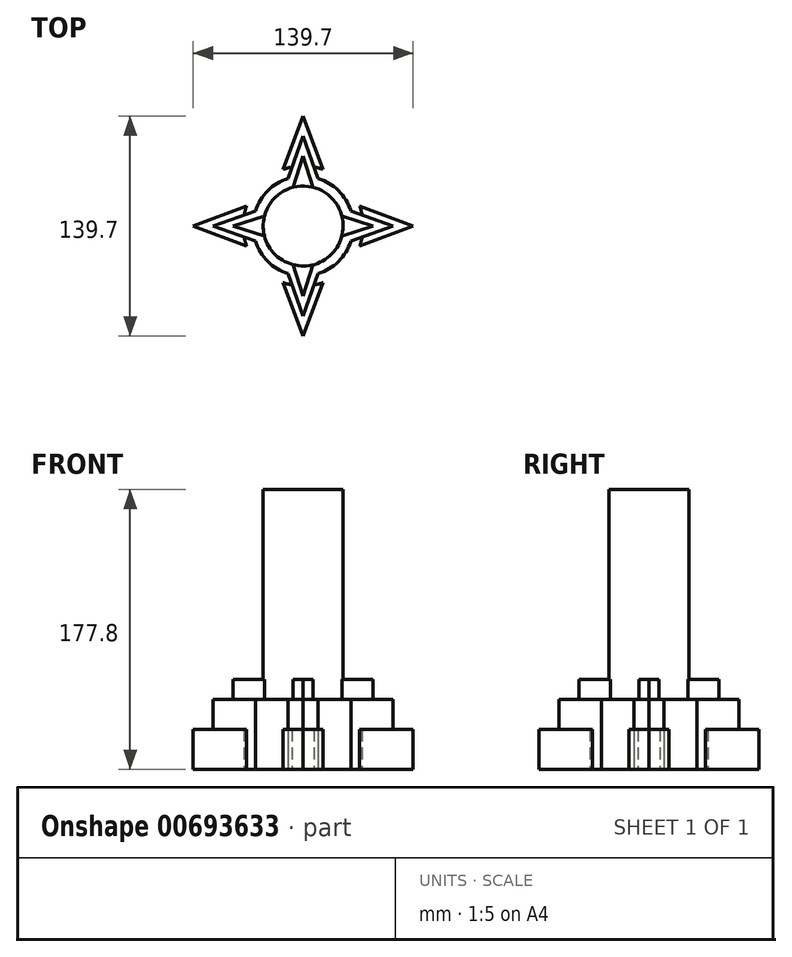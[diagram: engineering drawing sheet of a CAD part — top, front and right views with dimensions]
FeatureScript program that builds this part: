
annotation { "Feature Type Name" : "Feature", "Feature Type Description" : "" }
export const myFeature = defineFeature(function(context is Context, id is Id, definition is map)
    precondition{}
    {
        {
            var Q0;
            Q0=qCreatedBy(makeId("Top.planeOp"),FACE);
            var sketch = newSketch(context, id + "F0", { "sketchPlane" : qUnion([Q0])});
            skCircle(sketch, "E0", {"center": v(0, 0) * mm, "radius": 38.1 * mm});
            skLineSegment(sketch, "E1", {"start": v(-35.92, 12.7) * mm, "end": v(-69.85, 0) * mm});
            skLineSegment(sketch, "E2", {"start": v(-69.85, 0) * mm, "end": v(-35.92, -12.7) * mm});
            skLineSegment(sketch, "E3", {"start": v(-69.85, 0) * mm, "end": v(-38.1, 0) * mm});
            skLineSegment(sketch, "E4", {"start": v(-12.7, 35.92) * mm, "end": v(0, 69.85) * mm});
            skLineSegment(sketch, "E5", {"start": v(0, 38.1) * mm, "end": v(0, 69.85) * mm});
            skLineSegment(sketch, "E6.MirrorCS", {"start": v(12.7, 35.92) * mm, "end": v(0, 69.85) * mm});
            skLineSegment(sketch, "E7.MirrorCS", {"start": v(35.92, 12.7) * mm, "end": v(69.85, 0) * mm});
            skLineSegment(sketch, "E8.MirrorCS", {"start": v(69.85, 0) * mm, "end": v(35.92, -12.7) * mm});
            skLineSegment(sketch, "E9.MirrorCS", {"start": v(-12.7, -35.92) * mm, "end": v(0, -69.85) * mm});
            skLineSegment(sketch, "E10.MirrorCS", {"start": v(12.7, -35.92) * mm, "end": v(0, -69.85) * mm});
            skSolve(sketch);
        }
        {
            var Q0;
            {var subQ0=sQuery(id+"F0.wireOp",EDGE,"E1");Q0=makeQuery(id+"F0.imprint","IMPRINT",FACE,{"disambiguationData":[TD([[makeQuery(id+"F0.imprint","IMPRINT",EDGE,{"derivedFrom":subQ0}),1.0]])]});}
            var Q1;
            {var subQ0=sQuery(id+"F0.wireOp",EDGE,"E2");Q1=makeQuery(id+"F0.imprint","IMPRINT",FACE,{"disambiguationData":[TD([[makeQuery(id+"F0.imprint","IMPRINT",EDGE,{"derivedFrom":subQ0}),1.0]])]});}
            var Q2;
            {var subQ0=sQuery(id+"F0.wireOp",EDGE,"E7.MirrorCS");Q2=makeQuery(id+"F0.imprint","IMPRINT",FACE,{"disambiguationData":[TD([[makeQuery(id+"F0.imprint","IMPRINT",EDGE,{"derivedFrom":subQ0}),-1.0]])]});}
            var Q3;
            {var subQ0=sQuery(id+"F0.wireOp",EDGE,"E5");Q3=makeQuery(id+"F0.imprint","IMPRINT",FACE,{"disambiguationData":[TD([[makeQuery(id+"F0.imprint","IMPRINT",EDGE,{"derivedFrom":subQ0}),-1.0]])]});}
            var Q4;
            {var subQ0=sQuery(id+"F0.wireOp",EDGE,"E4");Q4=makeQuery(id+"F0.imprint","IMPRINT",FACE,{"disambiguationData":[TD([[makeQuery(id+"F0.imprint","IMPRINT",EDGE,{"derivedFrom":subQ0}),-1.0]])]});}
            var Q5;
            {var subQ0=sQuery(id+"F0.wireOp",EDGE,"E0");var subQ4=makeQuery(id+"F0.imprint","INTERSECT",VERTEX,{"derivedFrom":[sQuery(id+"F0.wireOp",EDGE,"E1"),subQ0]});Q5=makeQuery(id+"F0.imprint","IMPRINT",FACE,{"disambiguationData":[TD([[makeQuery(id+"F0.imprint","IMPRINT",EDGE,{"disambiguationData":[TD([[subQ4,1.0]])],"derivedFrom":subQ0}),-1.0]])]});}
            var Q6;
            {var subQ0=sQuery(id+"F0.wireOp",EDGE,"E9.MirrorCS");Q6=makeQuery(id+"F0.imprint","IMPRINT",FACE,{"disambiguationData":[TD([[makeQuery(id+"F0.imprint","IMPRINT",EDGE,{"derivedFrom":subQ0}),1.0]])]});}
            extrude(context, id + "F1", {"entities" : qUnion([Q0, Q1, Q2, Q3, Q4, Q5, Q6]), "depth" : 25.4 * mm, "offsetDistance" : 25.4 * mm});
        }
        {
            var Q0;
            Q0=qCreatedBy(makeId("Top.planeOp"),FACE);
            var sketch = newSketch(context, id + "F2", { "sketchPlane" : qUnion([Q0])});
            skCircle(sketch, "E11", {"center": v(0, 0) * mm, "radius": 31.75 * mm});
            skLineSegment(sketch, "E12", {"start": v(-30.29, 9.52) * mm, "end": v(-57.15, 0) * mm});
            skLineSegment(sketch, "E13", {"start": v(-57.15, 0) * mm, "end": v(-30.29, -9.53) * mm});
            skLineSegment(sketch, "E14", {"start": v(-57.15, 0) * mm, "end": v(-31.75, 0) * mm});
            skLineSegment(sketch, "E15.MirrorCS", {"start": v(57.15, 0) * mm, "end": v(30.29, -9.53) * mm});
            skLineSegment(sketch, "E16.MirrorCS", {"start": v(30.29, 9.52) * mm, "end": v(57.15, 0) * mm});
            skLineSegment(sketch, "E17", {"start": v(-9.52, -30.29) * mm, "end": v(0, -57.15) * mm});
            skLineSegment(sketch, "E18", {"start": v(0, -57.15) * mm, "end": v(9.52, -30.29) * mm});
            skLineSegment(sketch, "E19", {"start": v(0, -57.15) * mm, "end": v(0, -31.75) * mm});
            skLineSegment(sketch, "E20.MirrorCS", {"start": v(-9.52, 30.29) * mm, "end": v(0, 57.15) * mm});
            skLineSegment(sketch, "E21.MirrorCS", {"start": v(0, 57.15) * mm, "end": v(9.52, 30.29) * mm});
            skSolve(sketch);
        }
        {
            var Q0;
            Q0 = qSketchRegion(id + "F2", true);
            extrude(context, id + "F3", {"entities" : qUnion([Q0]), "operationType" : NewBodyOperationType.ADD, "depth" : 44.45 * mm, "offsetDistance" : 25.4 * mm});
        }
        {
            var Q0;
            Q0=qCreatedBy(makeId("Top.planeOp"),FACE);
            var sketch = newSketch(context, id + "F4", { "sketchPlane" : qUnion([Q0])});
            skCircle(sketch, "E22", {"center": v(0, 0) * mm, "radius": 25.4 * mm});
            skLineSegment(sketch, "E23", {"start": v(-24.6, 6.35) * mm, "end": v(-44.45, 0) * mm});
            skLineSegment(sketch, "E24", {"start": v(-44.45, 0) * mm, "end": v(-24.6, -6.35) * mm});
            skLineSegment(sketch, "E25", {"start": v(-44.45, 0) * mm, "end": v(-25.4, 0) * mm});
            skLineSegment(sketch, "E26.MirrorCS", {"start": v(44.45, 0) * mm, "end": v(24.6, -6.35) * mm});
            skLineSegment(sketch, "E27.MirrorCS", {"start": v(24.6, 6.35) * mm, "end": v(44.45, 0) * mm});
            skLineSegment(sketch, "E28", {"start": v(-6.35, 24.6) * mm, "end": v(0, 44.45) * mm});
            skLineSegment(sketch, "E29", {"start": v(0, 44.45) * mm, "end": v(6.35, 24.6) * mm});
            skLineSegment(sketch, "E30", {"start": v(0, 25.4) * mm, "end": v(0, 44.45) * mm});
            skLineSegment(sketch, "E31.MirrorCS", {"start": v(-6.35, -24.6) * mm, "end": v(0, -44.45) * mm});
            skLineSegment(sketch, "E32.MirrorCS", {"start": v(0, -44.45) * mm, "end": v(6.35, -24.6) * mm});
            skSolve(sketch);
        }
        {
            var Q0;
            Q0 = qSketchRegion(id + "F4", true);
            extrude(context, id + "F5", {"entities" : qUnion([Q0]), "operationType" : NewBodyOperationType.ADD, "depth" : 57.15 * mm, "offsetDistance" : 25.4 * mm});
        }
        {
            var Q0;
            Q0=qCreatedBy(makeId("Top.planeOp"),FACE);
            var sketch = newSketch(context, id + "F6", { "sketchPlane" : qUnion([Q0])});
            skCircle(sketch, "E33", {"center": v(0, 0) * mm, "radius": 25.4 * mm});
            skSolve(sketch);
        }
        {
            var Q0;
            Q0 = qSketchRegion(id + "F6", true);
            extrude(context, id + "F7", {"entities" : qUnion([Q0]), "operationType" : NewBodyOperationType.ADD, "depth" : 177.8 * mm, "offsetDistance" : 25.4 * mm});
        }
    });
